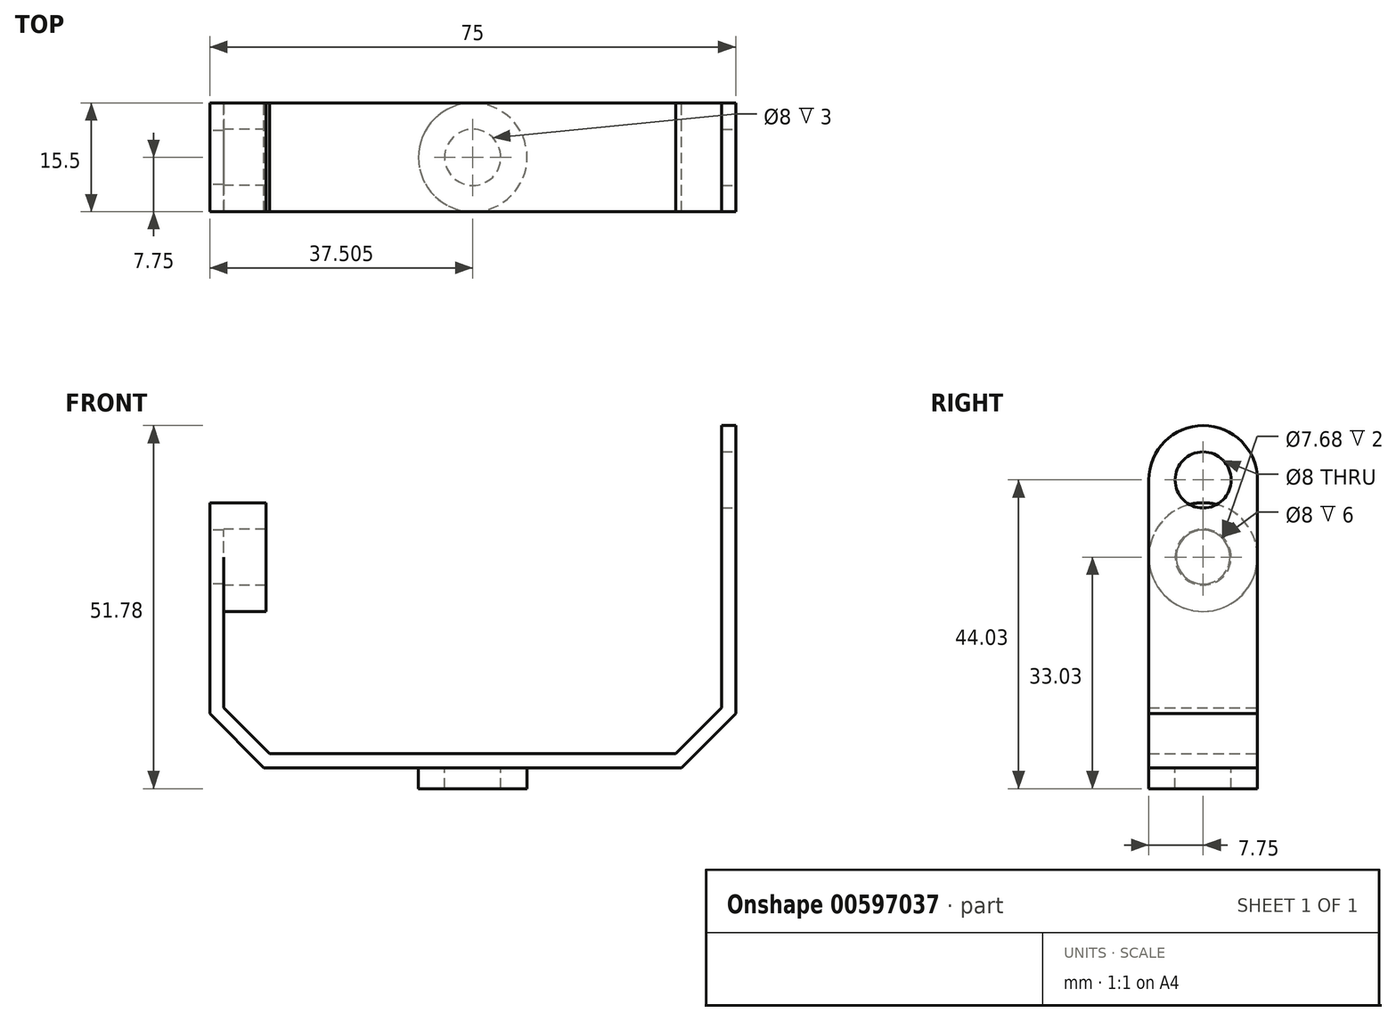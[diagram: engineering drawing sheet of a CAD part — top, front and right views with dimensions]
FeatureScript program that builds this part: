
annotation { "Feature Type Name" : "Feature", "Feature Type Description" : "" }
export const myFeature = defineFeature(function(context is Context, id is Id, definition is map)
    precondition{}
    {
        {
            var Q0;
            Q0=qCreatedBy(makeId("Front.planeOp"),FACE);
            var sketch = newSketch(context, id + "F0", { "sketchPlane" : qUnion([Q0])});
            skLineSegment(sketch, "E0", {"start": v(-14.47, 21.5) * mm, "end": v(-14.47, 0) * mm});
            skLineSegment(sketch, "E1", {"start": v(-14.47, 0) * mm, "end": v(-7.93, -6.53) * mm});
            skLineSegment(sketch, "E2", {"start": v(-7.93, -6.53) * mm, "end": v(50, -6.53) * mm});
            skLineSegment(sketch, "E3", {"start": v(50, -6.53) * mm, "end": v(56.53, 0) * mm});
            skLineSegment(sketch, "E4", {"start": v(56.53, 0) * mm, "end": v(56.53, 32.5) * mm});
            skLineSegment(sketch, "E5", {"start": v(-14.47, 21.5) * mm, "end": v(-16.47, 21.5) * mm});
            skLineSegment(sketch, "E6", {"start": v(-16.47, 21.5) * mm, "end": v(-16.47, -0.83) * mm});
            skLineSegment(sketch, "E7", {"start": v(-16.47, -0.83) * mm, "end": v(-8.76, -8.53) * mm});
            skLineSegment(sketch, "E8", {"start": v(-8.76, -8.53) * mm, "end": v(50.83, -8.53) * mm});
            skLineSegment(sketch, "E9", {"start": v(50.83, -8.53) * mm, "end": v(58.53, -0.83) * mm});
            skLineSegment(sketch, "E10", {"start": v(56.53, 32.5) * mm, "end": v(58.53, 32.5) * mm});
            skLineSegment(sketch, "E11", {"start": v(58.53, 32.5) * mm, "end": v(58.53, -0.83) * mm});
            skSolve(sketch);
        }
        {
            var Q0;
            Q0 = qSketchRegion(id + "F0", true);
            extrude(context, id + "F1", {"entities" : qUnion([Q0]), "endBound" : BoundingType.SYMMETRIC, "depth" : 15.5 * mm, "offsetDistance" : 25.4 * mm});
        }
        {
            var Q0;
            Q0=makeQuery(id+"F1.opExtrude","SWEPT_FACE",FACE,{"disambiguationData":[OSD([sQuery(id+"F0.wireOp",EDGE,"E6")])]});
            var sketch = newSketch(context, id + "F2", { "sketchPlane" : qUnion([Q0])});
            skCircle(sketch, "E12", {"center": v(0, 21.5) * mm, "radius": 7.75 * mm});
            skLineSegment(sketch, "E13", {"start": v(-7.75, 21.5) * mm, "end": v(7.75, 21.5) * mm});
            skSolve(sketch);
        }
        {
            var Q0;
            {var subQ0=sQuery(id+"F2.wireOp",EDGE,"E13");Q0=makeQuery(id+"F2.imprint","IMPRINT",FACE,{"disambiguationData":[TD([[makeQuery(id+"F2.imprint","IMPRINT",EDGE,{"derivedFrom":subQ0}),-1.0]])]});}
            extrude(context, id + "F3", {"entities" : qUnion([Q0]), "operationType" : NewBodyOperationType.ADD, "oppositeDirection" : true, "depth" : 2 * mm, "offsetDistance" : 25.4 * mm});
        }
        {
            var Q0;
            Q0=makeQuery(id+"F3.boolean.opBoolean","MERGE",FACE,{"derivedFrom":[makeQuery(id+"F1.opExtrude","SWEPT_FACE",FACE,{"disambiguationData":[OSD([sQuery(id+"F0.wireOp",EDGE,"E6")])]}),makeQuery(id+"F3.opExtrude","CAP_FACE",FACE,{"disambiguationData":[OSD([sQuery(id+"F2.wireOp",EDGE,"E12"),sQuery(id+"F2.wireOp",EDGE,"E13")])],"isStart":true})]});
            var sketch = newSketch(context, id + "F4", { "sketchPlane" : qUnion([Q0])});
            skCircle(sketch, "E14", {"center": v(0, 21.5) * mm, "radius": 3.84 * mm});
            skSolve(sketch);
        }
        {
            var Q0;
            Q0 = qSketchRegion(id + "F4", true);
            extrude(context, id + "F5", {"entities" : qUnion([Q0]), "operationType" : NewBodyOperationType.REMOVE, "oppositeDirection" : true, "depth" : 25.4 * mm, "offsetDistance" : 25.4 * mm});
        }
        {
            var Q0;
            Q0=makeQuery(id+"F1.opExtrude","SWEPT_FACE",FACE,{"disambiguationData":[OSD([sQuery(id+"F0.wireOp",EDGE,"E11")])]});
            var sketch = newSketch(context, id + "F6", { "sketchPlane" : qUnion([Q0])});
            skCircle(sketch, "E15", {"center": v(0, 32.5) * mm, "radius": 7.75 * mm});
            skSolve(sketch);
        }
        {
            var Q0;
            {var subQ1=sQuery(id+"F0.wireOp",EDGE,"E11");var subQ2=makeQuery(id+"F1.opExtrude","SWEPT_EDGE",EDGE,{"disambiguationData":[OSD([sQuery(id+"F0.wireOp",EDGE,"E10"),subQ1])]});Q0=makeQuery(id+"F6.imprint","IMPRINT",FACE,{"disambiguationData":[TD([[makeQuery(id+"F6.imprint","IMPRINT",EDGE,{"derivedFrom":subQ2}),1.0]])]});}
            extrude(context, id + "F7", {"entities" : qUnion([Q0]), "operationType" : NewBodyOperationType.ADD, "oppositeDirection" : true, "depth" : 2 * mm, "offsetDistance" : 25.4 * mm});
        }
        {
            var Q0;
            {var subQ0=sQuery(id+"F0.wireOp",EDGE,"E11");Q0=makeQuery(id+"F7.boolean.opBoolean","MERGE",FACE,{"derivedFrom":[makeQuery(id+"F1.opExtrude","SWEPT_FACE",FACE,{"disambiguationData":[OSD([subQ0])]}),makeQuery(id+"F7.opExtrude","CAP_FACE",FACE,{"disambiguationData":[OSD([sQuery(id+"F0.wireOp",EDGE,"E10"),subQ0,sQuery(id+"F6.wireOp",EDGE,"E15")])],"isStart":true})]});}
            var sketch = newSketch(context, id + "F8", { "sketchPlane" : qUnion([Q0])});
            skCircle(sketch, "E16", {"center": v(0, 32.5) * mm, "radius": 4 * mm});
            skSolve(sketch);
        }
        {
            var Q0;
            Q0=makeQuery(id+"F8.imprint","IMPRINT",FACE,{"disambiguationData":[TD([[makeQuery(id+"F8.imprint","IMPRINT",EDGE,{"derivedFrom":sQuery(id+"F8.wireOp",EDGE,"E16")}),1.0]])]});
            extrude(context, id + "F9", {"entities" : qUnion([Q0]), "operationType" : NewBodyOperationType.REMOVE, "oppositeDirection" : true, "depth" : 25.4 * mm, "offsetDistance" : 25.4 * mm});
        }
        {
            var Q0;
            Q0=makeQuery(id+"F3.boolean.opBoolean","MERGE",FACE,{"derivedFrom":[makeQuery(id+"F1.opExtrude","SWEPT_FACE",FACE,{"disambiguationData":[OSD([sQuery(id+"F0.wireOp",EDGE,"E0")])]}),makeQuery(id+"F3.opExtrude","CAP_FACE",FACE,{"disambiguationData":[OSD([sQuery(id+"F2.wireOp",EDGE,"E12"),sQuery(id+"F2.wireOp",EDGE,"E13")])],"isStart":false})]});
            var sketch = newSketch(context, id + "F10", { "sketchPlane" : qUnion([Q0])});
            skCircle(sketch, "E17", {"center": v(0, 21.5) * mm, "radius": 4 * mm});
            skCircle(sketch, "E18", {"center": v(0, 21.5) * mm, "radius": 7.75 * mm});
            skSolve(sketch);
        }
        {
            var Q0;
            Q0 = qSketchRegion(id + "F10", true);
            extrude(context, id + "F11", {"entities" : qUnion([Q0]), "operationType" : NewBodyOperationType.ADD, "depth" : 6 * mm, "offsetDistance" : 25.4 * mm});
        }
        {
            var Q0;
            Q0=makeQuery(id+"F1.opExtrude","SWEPT_FACE",FACE,{"disambiguationData":[OSD([sQuery(id+"F0.wireOp",EDGE,"E8")])]});
            var sketch = newSketch(context, id + "F12", { "sketchPlane" : qUnion([Q0])});
            skLineSegment(sketch, "E19.bottom", {"start": v(-8.76, 7.75) * mm, "end": v(50.83, 7.75) * mm});
            skLineSegment(sketch, "E19.top", {"start": v(-8.76, -7.75) * mm, "end": v(50.83, -7.75) * mm});
            skLineSegment(sketch, "E19.left", {"start": v(-8.76, 7.75) * mm, "end": v(-8.76, -7.75) * mm});
            skLineSegment(sketch, "E19.right", {"start": v(50.83, 7.75) * mm, "end": v(50.83, -7.75) * mm});
            skPoint(sketch, "E19.middle", {"position": v(21.03, 0) * mm});
            skPoint(sketch, "E19.middle.positionSnap0", {"position": v(21.03, 7.75) * mm});
            skPoint(sketch, "E19.centerSnap0", {"position": v(21.03, 7.75) * mm});
            skCircle(sketch, "E20", {"center": v(21.03, 0) * mm, "radius": 4 * mm});
            skCircle(sketch, "E21", {"center": v(21.03, 0) * mm, "radius": 7.75 * mm});
            skSolve(sketch);
        }
        {
            var Q0;
            Q0=makeQuery(id+"F12.imprint","IMPRINT",FACE,{"disambiguationData":[TD([[makeQuery(id+"F12.imprint","IMPRINT",EDGE,{"derivedFrom":sQuery(id+"F12.wireOp",EDGE,"E20")}),-1.0]])]});
            extrude(context, id + "F13", {"entities" : qUnion([Q0]), "operationType" : NewBodyOperationType.ADD, "depth" : 3 * mm, "offsetDistance" : 25.4 * mm});
        }
    });
